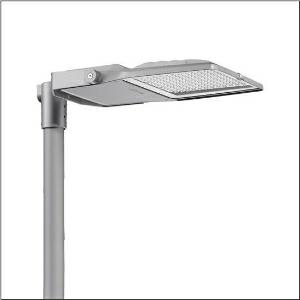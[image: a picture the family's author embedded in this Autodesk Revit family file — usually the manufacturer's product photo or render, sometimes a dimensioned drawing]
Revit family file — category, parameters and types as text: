
# Revit family: floodlight_fl_21_iq_midi___pl43_5xa7781e2a3a_1390
name_source: partatom
category: Lighting Fixtures
units: mm (PartAtom-declared; Revit-internal decimal feet)

## family parameters
Cut with Voids When Loaded = No
Host = Face
Light Source = No
Part Type = Normal
Room Calculation Point = No
Round Connector Dimension = Use Diameter
Shared = No

## types (1)
- --- (1 x LED, 27540 lm, 208.1 W, 3000K)
    Apparent Load = 208 VA
    CIE Flux Codes = 27 78 99 100 100
    Color Rendering = 70
    Color Temperature = 3000K
    Default Elevation = 1800 mm
    Description = Floodlight FL 21 iQ midi, floodlight, primary light control with lens, of PMMA, primary optical cover: protective disc, of toughened safety glass, transparent, light distribution: PL43, light emission: direct distribution, installation type: surface-mounted, LED, High Power LED, rated luminous flux: 27.540lm, luminous efficacy: 132lm/W, light colour: 730, colour temperature: 3000K, control gear: iQ Comfort/DALI, control: optimised constant luminous flux control (CLO 2.0), Desk-Remote (wireless, voltage-free reading and setting of iQ features in the workshop via application-optimized NFC function/RFID function), Light-Fading, Smart-Wire, Night-Set, Lumen-Switch, Temp-Guard, Auto-Match, with terminal, 6-pole, mains connection: 220..240V, AC, 50/60Hz, start of lifetime: 208W, end of service life: 227W, reduction: 90W, luminaire housing, of diecast aluminium, powder-coated, Siteco® metallic grey (DB 702S), corrosivity category C5 mid according to DIN EN ISO 12944, suitable for swimming pools, chlorine-resistant, sealing non-destructively replaceable, please order mast flange separately, mast bracket, of steel, galvanised, powder-coated, Siteco® metallic grey (DB 702S), protection rating (complete): IP66, insulation class (complete): insulation class II (safety insulation), certification: CE, ENEC, VDE, protection symbol: D, impact resistance: IK08, permissible operating ambient temperature: -40..+40°C, permissible operating ambient temperature for outdoor applications: -40..+50°C, standard: DIN EN 12944, LABS conformity tested according to VDMA 24364:2018-05, packaging unit: 1 piece

Light Distribution: PL43
    Height = 76 mm
    Lamp = 1 x LED
    Lamp Light Flux = 27540 lm
    Lamp Power = 208.1 W
    Lamp count = 1
    Length = 657 mm
    Luminous efficacy = 132 lm/W
    Manufacturer = Siteco
    ModVariant = No
    Model = 5XA7781E2A3A
    Number of Poles = 1
    OnlyDefault = Yes
    Power Factor = 1
    Product Name = Floodlight FL 21 iQ midi | PL43
    Product group = floodlight | pylon annexe
    ProductGroupID = 6200
    Protection Class = Protection class II
    Protection Degree = IP 66
    RLX_Detail_Level = 1
    RLX_Emergency_Light_Flux = 0 lm
    RLX_Emergency_Type = 0
    RLX_Emergency_Type_DB = No
    RlxData = <blob elided: 153529 chars, md5=901c8963>
    Socket = socket
    Standby Power = 0 W
    System Light Flux = 27540 lm
    System Power = 208 W
    Type Comments = factory setting: luminous flux: 100 % | dim-lin: 254 | 710 mA
    Type Image = l_1007123.jpg
    URL = http://relux.com
    VarID = @adj_105376
    Voltage = 0 V
    Weight = 0.00 kg
    Width = 442 mm

## geometry (parser evidence)
native form markers: Blend x4, Sweep x14
no freeform markers — native parametric forms only
